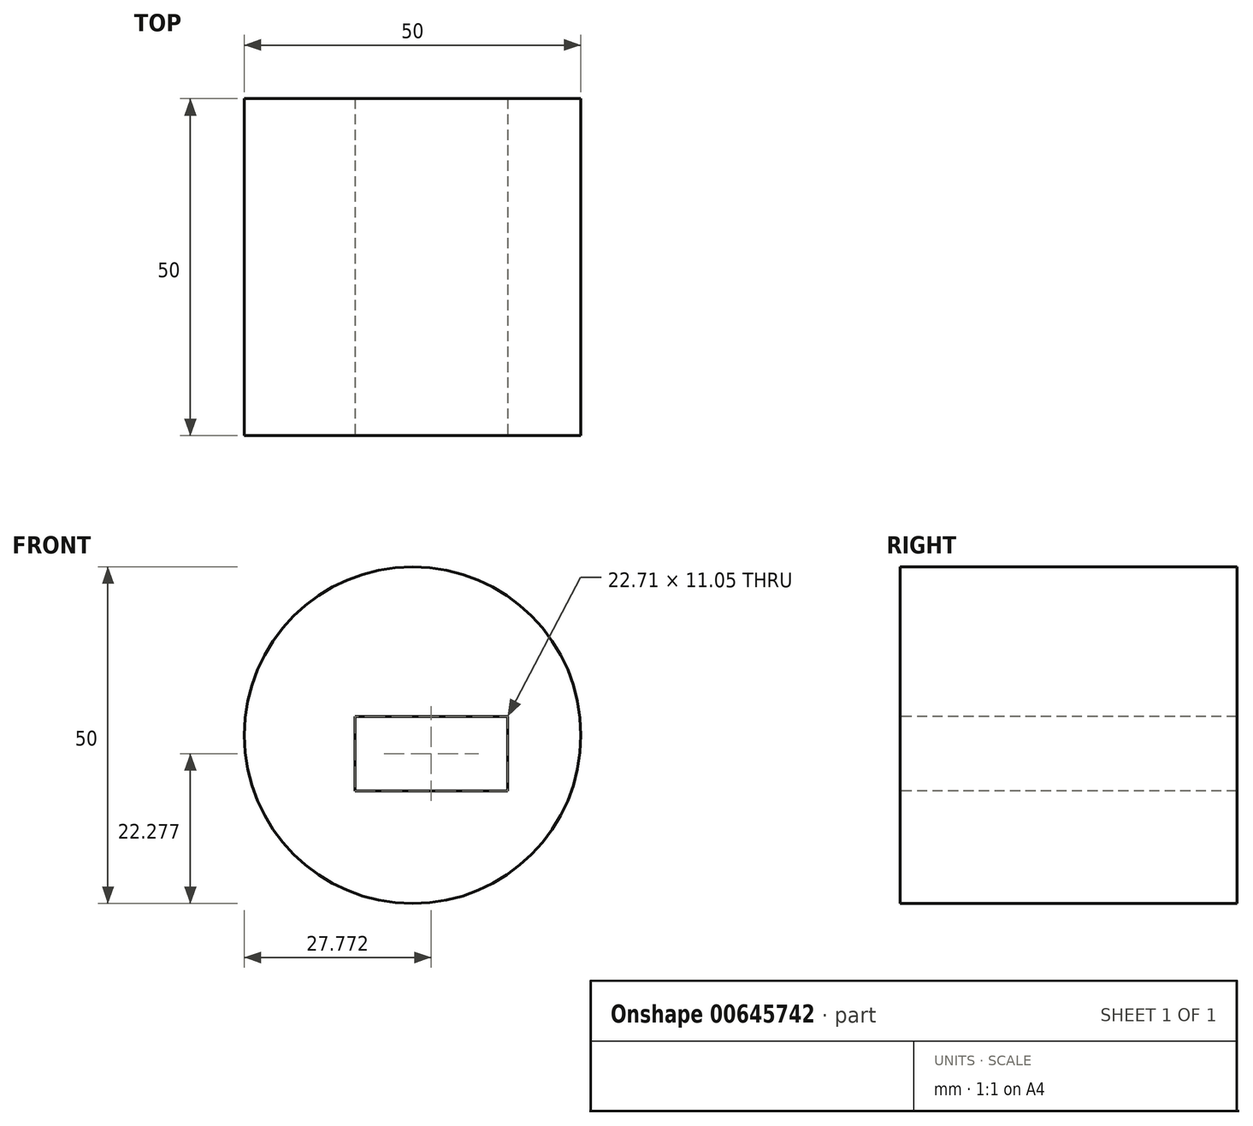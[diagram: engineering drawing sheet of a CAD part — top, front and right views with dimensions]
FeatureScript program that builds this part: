
annotation { "Feature Type Name" : "Feature", "Feature Type Description" : "" }
export const myFeature = defineFeature(function(context is Context, id is Id, definition is map)
    precondition{}
    {
        {
            var Q0;
            Q0=qCreatedBy(makeId("Front.planeOp"),FACE);
            var sketch = newSketch(context, id + "F0", { "sketchPlane" : qUnion([Q0])});
            skCircle(sketch, "E0", {"center": v(0, 0) * mm, "radius": 25 * mm});
            skSolve(sketch);
        }
        {
            var Q0;
            Q0=makeQuery(id+"F0.imprint","IMPRINT",FACE,{"disambiguationData":[TD([[makeQuery(id+"F0.imprint","IMPRINT",EDGE,{"derivedFrom":sQuery(id+"F0.wireOp",EDGE,"E0")}),1.0]])]});
            extrude(context, id + "F1", {"entities" : qUnion([Q0]), "depth" : 50 * mm, "offsetDistance" : 25 * mm});
        }
        {
            var Q0;
            Q0=makeQuery(id+"F1.opExtrude","CAP_FACE",FACE,{"disambiguationData":[OSD([sQuery(id+"F0.wireOp",EDGE,"E0")])],"isStart":false});
            var sketch = newSketch(context, id + "F2", { "sketchPlane" : qUnion([Q0])});
            skLineSegment(sketch, "E1.bottom", {"start": v(-8.58, 2.8) * mm, "end": v(14.13, 2.8) * mm});
            skLineSegment(sketch, "E1.top", {"start": v(-8.58, -8.25) * mm, "end": v(14.13, -8.25) * mm});
            skLineSegment(sketch, "E1.left", {"start": v(-8.58, 2.8) * mm, "end": v(-8.58, -8.25) * mm});
            skLineSegment(sketch, "E1.right", {"start": v(14.13, 2.8) * mm, "end": v(14.13, -8.25) * mm});
            skSolve(sketch);
        }
        {
            var Q0;
            Q0=makeQuery(id+"F2.imprint","IMPRINT",FACE,{"disambiguationData":[TD([[makeQuery(id+"F2.imprint","IMPRINT",EDGE,{"derivedFrom":sQuery(id+"F2.wireOp",EDGE,"E1.bottom")}),-1.0]])]});
            extrude(context, id + "F3", {"entities" : qUnion([Q0]), "operationType" : NewBodyOperationType.REMOVE, "endBound" : BoundingType.THROUGH_ALL, "oppositeDirection" : true, "depth" : 25 * mm, "offsetDistance" : 25 * mm});
        }
    });
